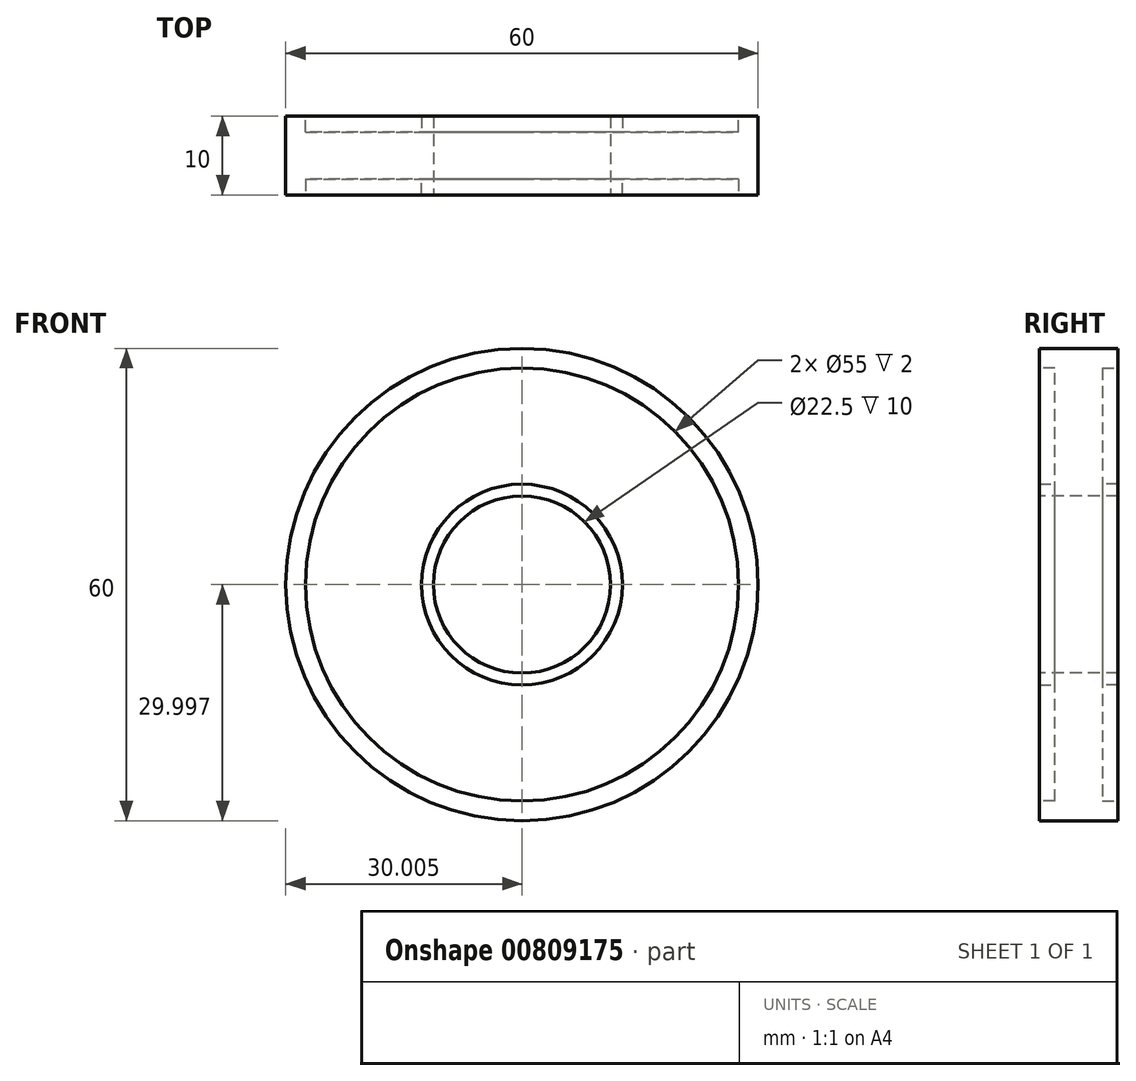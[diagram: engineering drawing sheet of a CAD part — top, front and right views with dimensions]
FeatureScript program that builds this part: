
annotation { "Feature Type Name" : "Feature", "Feature Type Description" : "" }
export const myFeature = defineFeature(function(context is Context, id is Id, definition is map)
    precondition{}
    {
        {
            var Q0;
            Q0=qCreatedBy(makeId("Front.planeOp"),FACE);
            var sketch = newSketch(context, id + "F0", { "sketchPlane" : qUnion([Q0])});
            skCircle(sketch, "E0", {"center": v(-21.97, 3.42) * mm, "radius": 30 * mm});
            skSolve(sketch);
        }
        {
            var Q0;
            Q0 = qSketchRegion(id + "F0", true);
            extrude(context, id + "F1", {"entities" : qUnion([Q0]), "depth" : 10 * mm, "offsetDistance" : 25 * mm});
        }
        {
            var Q0;
            Q0=makeQuery(id+"F1.opExtrude","CAP_FACE",FACE,{"disambiguationData":[OSD([sQuery(id+"F0.wireOp",EDGE,"E0")])],"isStart":false});
            var sketch = newSketch(context, id + "F2", { "sketchPlane" : qUnion([Q0])});
            skCircle(sketch, "E1", {"center": v(-21.97, 3.42) * mm, "radius": 27.5 * mm});
            skSolve(sketch);
        }
        {
            var Q0;
            Q0 = qSketchRegion(id + "F2", true);
            extrude(context, id + "F3", {"entities" : qUnion([Q0]), "operationType" : NewBodyOperationType.REMOVE, "oppositeDirection" : true, "depth" : 2 * mm, "offsetDistance" : 25 * mm});
        }
        {
            var Q0;
            Q0=makeQuery(id+"F1.opExtrude","CAP_FACE",FACE,{"disambiguationData":[OSD([sQuery(id+"F0.wireOp",EDGE,"E0")])],"isStart":true});
            var sketch = newSketch(context, id + "F4", { "sketchPlane" : qUnion([Q0])});
            skCircle(sketch, "E2", {"center": v(21.97, 3.42) * mm, "radius": 27.5 * mm});
            skSolve(sketch);
        }
        {
            var Q0;
            Q0 = qSketchRegion(id + "F4", true);
            extrude(context, id + "F5", {"entities" : qUnion([Q0]), "operationType" : NewBodyOperationType.REMOVE, "oppositeDirection" : true, "depth" : 2 * mm, "offsetDistance" : 25 * mm});
        }
        {
            var Q0;
            Q0=makeQuery(id+"F5.boolean.opBoolean","COPY",FACE,{"derivedFrom":makeQuery(id+"F5.opExtrude","CAP_FACE",FACE,{"disambiguationData":[OSD([sQuery(id+"F4.wireOp",EDGE,"E2")])],"isStart":false})});
            var sketch = newSketch(context, id + "F6", { "sketchPlane" : qUnion([Q0])});
            skCircle(sketch, "E3", {"center": v(21.97, 3.42) * mm, "radius": 12.75 * mm});
            skSolve(sketch);
        }
        {
            var Q0;
            Q0 = qSketchRegion(id + "F6", true);
            extrude(context, id + "F7", {"entities" : qUnion([Q0]), "operationType" : NewBodyOperationType.ADD, "depth" : 2 * mm, "offsetDistance" : 25 * mm});
        }
        {
            var Q0;
            Q0=makeQuery(id+"F3.boolean.opBoolean","COPY",FACE,{"derivedFrom":makeQuery(id+"F3.opExtrude","CAP_FACE",FACE,{"disambiguationData":[OSD([sQuery(id+"F2.wireOp",EDGE,"E1")])],"isStart":false})});
            var sketch = newSketch(context, id + "F8", { "sketchPlane" : qUnion([Q0])});
            skCircle(sketch, "E4", {"center": v(-21.97, 3.42) * mm, "radius": 12.75 * mm});
            skSolve(sketch);
        }
        {
            var Q0;
            Q0 = qSketchRegion(id + "F8", true);
            extrude(context, id + "F9", {"entities" : qUnion([Q0]), "operationType" : NewBodyOperationType.ADD, "depth" : 2 * mm, "offsetDistance" : 25 * mm});
        }
        {
            var Q0;
            Q0=makeQuery(id+"F9.opExtrude","CAP_FACE",FACE,{"disambiguationData":[OSD([sQuery(id+"F8.wireOp",EDGE,"E4")])],"isStart":false});
            var sketch = newSketch(context, id + "F10", { "sketchPlane" : qUnion([Q0])});
            skCircle(sketch, "E5", {"center": v(-21.97, 3.42) * mm, "radius": 11.25 * mm});
            skSolve(sketch);
        }
        {
            var Q0;
            Q0 = qSketchRegion(id + "F10", true);
            extrude(context, id + "F11", {"entities" : qUnion([Q0]), "operationType" : NewBodyOperationType.REMOVE, "endBound" : BoundingType.THROUGH_ALL, "oppositeDirection" : true, "depth" : 25 * mm, "offsetDistance" : 25 * mm});
        }
    });
